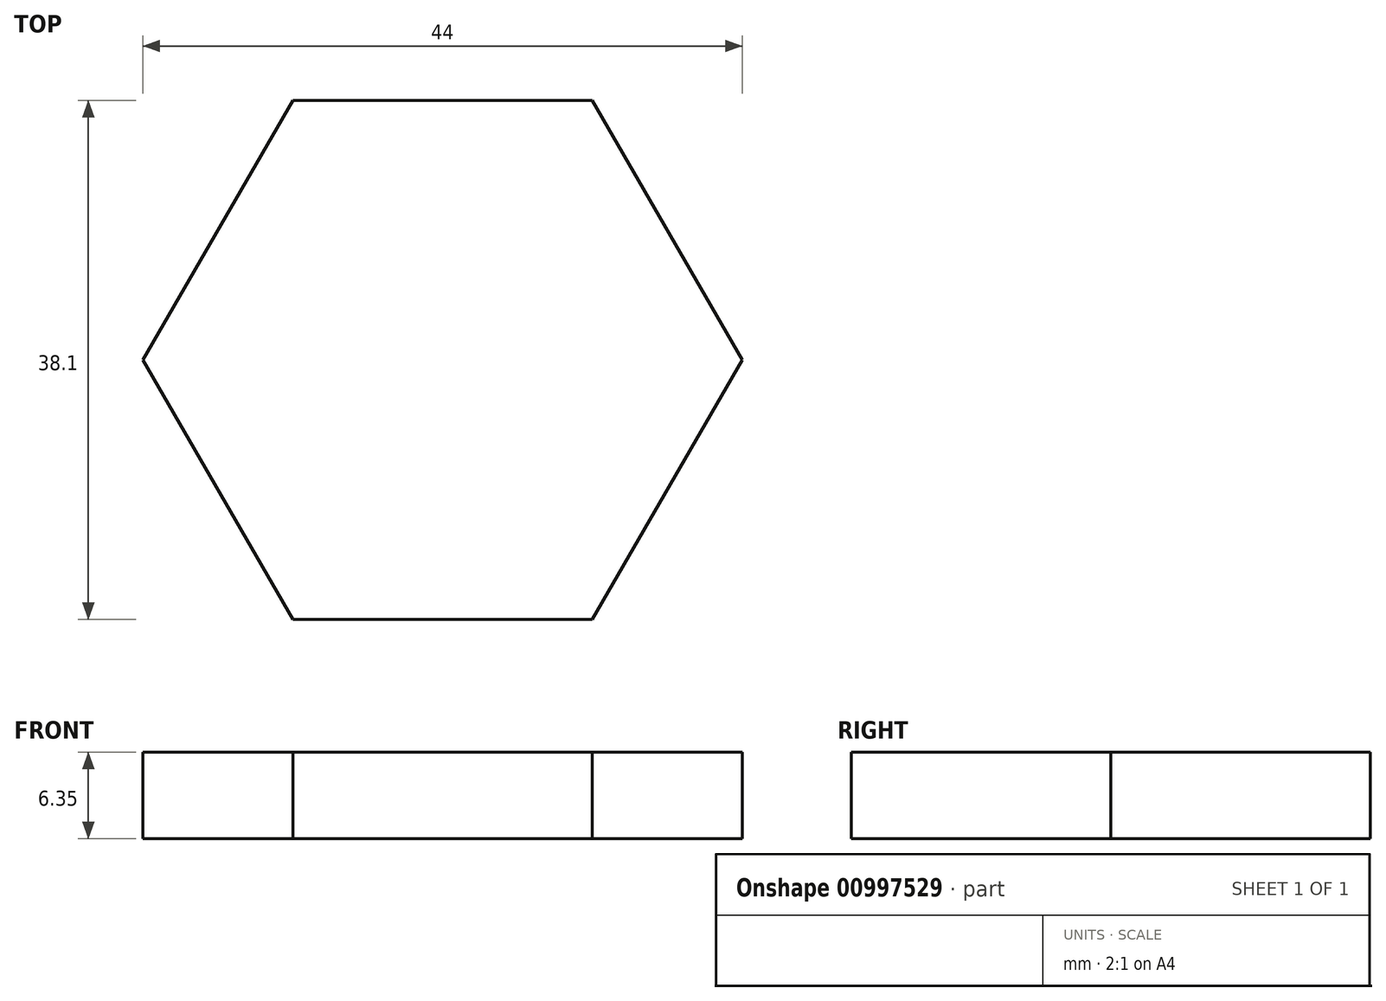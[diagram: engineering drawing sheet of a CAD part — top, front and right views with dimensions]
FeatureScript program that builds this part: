
annotation { "Feature Type Name" : "Feature", "Feature Type Description" : "" }
export const myFeature = defineFeature(function(context is Context, id is Id, definition is map)
    precondition{}
    {
        {
            var Q0;
            Q0=qCreatedBy(makeId("Top.planeOp"),FACE);
            var sketch = newSketch(context, id + "F0", { "sketchPlane" : qUnion([Q0])});
            skCircle(sketch, "E0.cCircle", {"center": v(0, 0) * mm, "radius": 19.05 * mm, "construction": true});
            skLineSegment(sketch, "E0.0", {"start": v(-22, 0) * mm, "end": v(-11, 19.05) * mm});
            skLineSegment(sketch, "E0.1", {"start": v(-11, 19.05) * mm, "end": v(11, 19.05) * mm});
            skLineSegment(sketch, "E0.2", {"start": v(11, 19.05) * mm, "end": v(22, 0) * mm});
            skLineSegment(sketch, "E0.3", {"start": v(22, 0) * mm, "end": v(11, -19.05) * mm});
            skLineSegment(sketch, "E0.4", {"start": v(11, -19.05) * mm, "end": v(-11, -19.05) * mm});
            skLineSegment(sketch, "E0.5", {"start": v(-11, -19.05) * mm, "end": v(-22, 0) * mm});
            skPoint(sketch, "E0.0.midPoint", {"position": v(-16.5, 9.53) * mm});
            skSolve(sketch);
        }
        {
            var Q0;
            Q0 = qSketchRegion(id + "F0", true);
            extrude(context, id + "F1", {"entities" : qUnion([Q0]), "depth" : 6.35 * mm, "offsetDistance" : 25.4 * mm});
        }
    });
